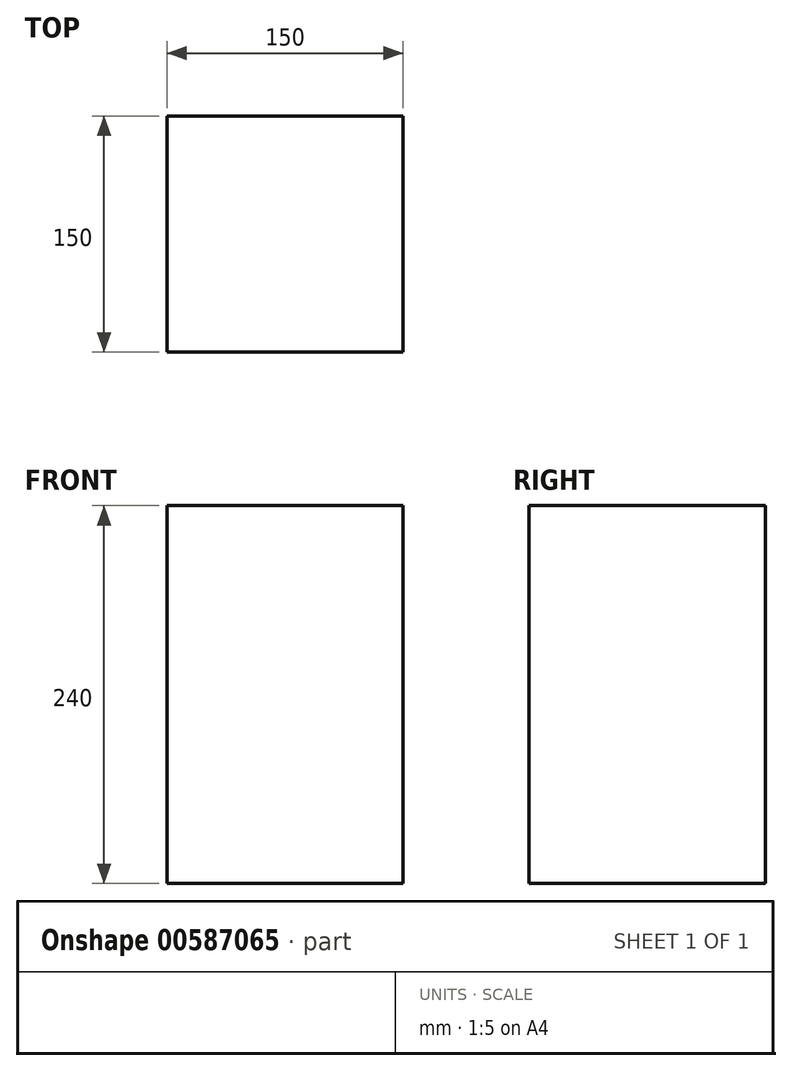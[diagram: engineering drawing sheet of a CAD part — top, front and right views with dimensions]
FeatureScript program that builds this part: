
annotation { "Feature Type Name" : "Feature", "Feature Type Description" : "" }
export const myFeature = defineFeature(function(context is Context, id is Id, definition is map)
    precondition{}
    {
        {
            var Q0;
            Q0=qCreatedBy(makeId("Top.planeOp"),FACE);
            var sketch = newSketch(context, id + "F0", { "sketchPlane" : qUnion([Q0])});
            skLineSegment(sketch, "E0.bottom", {"start": v(0, 0) * mm, "end": v(150, 0) * mm});
            skLineSegment(sketch, "E0.top", {"start": v(0, 150) * mm, "end": v(150, 150) * mm});
            skLineSegment(sketch, "E0.left", {"start": v(0, 0) * mm, "end": v(0, 150) * mm});
            skLineSegment(sketch, "E0.right", {"start": v(150, 0) * mm, "end": v(150, 150) * mm});
            skSolve(sketch);
        }
        {
            var Q0;
            Q0 = qSketchRegion(id + "F0", true);
            extrude(context, id + "F1", {"entities" : qUnion([Q0]), "depth" : 240 * mm, "offsetDistance" : 25 * mm});
        }
    });
